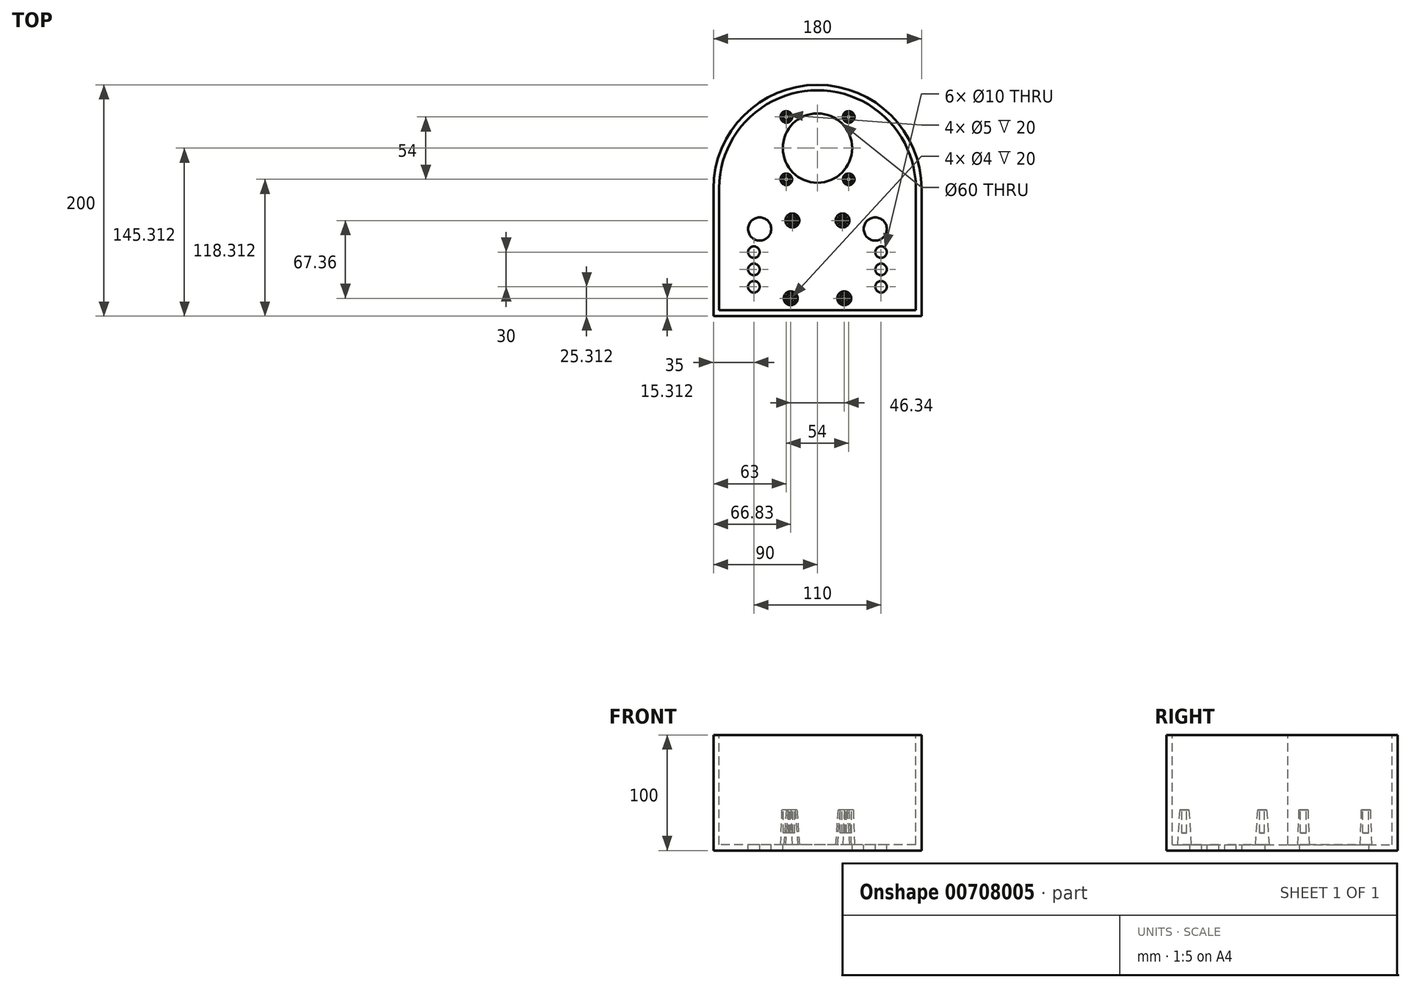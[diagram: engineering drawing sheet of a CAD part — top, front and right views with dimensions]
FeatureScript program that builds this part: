
annotation { "Feature Type Name" : "Feature", "Feature Type Description" : "" }
export const myFeature = defineFeature(function(context is Context, id is Id, definition is map)
    precondition{}
    {
        {
            var Q0;
            Q0=qCreatedBy(makeId("Top.planeOp"),FACE);
            var sketch = newSketch(context, id + "F0", { "sketchPlane" : qUnion([Q0])});
            skLineSegment(sketch, "E0.bottom", {"start": v(90, -55) * mm, "end": v(-90, -55) * mm});
            skLineSegment(sketch, "E0.top", {"start": v(90, 55) * mm, "end": v(-90, 55) * mm});
            skLineSegment(sketch, "E0.left", {"start": v(90, -55) * mm, "end": v(90, 55) * mm});
            skLineSegment(sketch, "E0.right", {"start": v(-90, -55) * mm, "end": v(-90, 55) * mm});
            skPoint(sketch, "E0.middle", {"position": v(0, 0) * mm});
            skArc(sketch, "E1", {"start": v(90, 55) * mm, "mid": v(0, 145) * mm, "end": v(-90, 55) * mm});
            skSolve(sketch);
        }
        {
            var Q0;
            Q0 = qSketchRegion(id + "F0", true);
            extrude(context, id + "F1", {"entities" : qUnion([Q0]), "depth" : 100 * mm, "offsetDistance" : 25 * mm});
        }
        {
            var Q0;
            Q0=makeQuery(id+"F1.opExtrude","CAP_FACE",FACE,{"disambiguationData":[OSD([sQuery(id+"F0.wireOp",EDGE,"E0.bottom"),sQuery(id+"F0.wireOp",EDGE,"E0.left"),sQuery(id+"F0.wireOp",EDGE,"E0.right"),sQuery(id+"F0.wireOp",EDGE,"E1")])],"isStart":false});
            var sketch = newSketch(context, id + "F2", { "sketchPlane" : qUnion([Q0])});
            skLineSegment(sketch, "E2.bottom", {"start": v(85, -50) * mm, "end": v(-85, -50) * mm});
            skLineSegment(sketch, "E2.top", {"start": v(85, 50) * mm, "end": v(-85, 50) * mm});
            skLineSegment(sketch, "E2.left", {"start": v(85, -50) * mm, "end": v(85, 50) * mm});
            skLineSegment(sketch, "E2.right", {"start": v(-85, -50) * mm, "end": v(-85, 50) * mm});
            skPoint(sketch, "E2.middle", {"position": v(0, 0) * mm});
            skArc(sketch, "E3", {"start": v(85, 50) * mm, "mid": v(0, 140.31) * mm, "end": v(-85, 50) * mm});
            skSolve(sketch);
        }
        {
            var Q0;
            Q0 = qSketchRegion(id + "F2", true);
            extrude(context, id + "F3", {"entities" : qUnion([Q0]), "operationType" : NewBodyOperationType.REMOVE, "oppositeDirection" : true, "depth" : 95 * mm, "offsetDistance" : 25 * mm});
        }
        {
            var Q0;
            Q0=makeQuery(id+"F3.boolean.opBoolean","COPY",FACE,{"derivedFrom":makeQuery(id+"F3.opExtrude","CAP_FACE",FACE,{"disambiguationData":[OSD([sQuery(id+"F2.wireOp",EDGE,"E2.bottom"),sQuery(id+"F2.wireOp",EDGE,"E2.left"),sQuery(id+"F2.wireOp",EDGE,"E2.right"),sQuery(id+"F2.wireOp",EDGE,"E3")])],"isStart":false})});
            var sketch = newSketch(context, id + "F4", { "sketchPlane" : qUnion([Q0])});
            skCircle(sketch, "E4", {"center": v(0, 90.31) * mm, "radius": 30 * mm});
            skCircle(sketch, "E5", {"center": v(-55, 0.31) * mm, "radius": 5 * mm});
            skCircle(sketch, "E6", {"center": v(-55, -14.69) * mm, "radius": 5 * mm});
            skCircle(sketch, "E7", {"center": v(55, 0.31) * mm, "radius": 5 * mm});
            skCircle(sketch, "E8", {"center": v(55, -14.69) * mm, "radius": 5 * mm});
            skCircle(sketch, "E9", {"center": v(-50, 20.31) * mm, "radius": 10 * mm});
            skCircle(sketch, "E10", {"center": v(50, 20.31) * mm, "radius": 10 * mm});
            skCircle(sketch, "E11", {"center": v(-55, -29.69) * mm, "radius": 5 * mm});
            skCircle(sketch, "E12", {"center": v(55, -29.69) * mm, "radius": 5 * mm});
            skSolve(sketch);
        }
        {
            var Q0;
            Q0 = qSketchRegion(id + "F4", true);
            extrude(context, id + "F5", {"entities" : qUnion([Q0]), "operationType" : NewBodyOperationType.REMOVE, "endBound" : BoundingType.THROUGH_ALL, "oppositeDirection" : true, "depth" : 25 * mm, "offsetDistance" : 25 * mm});
        }
        {
            var Q0;
            Q0=makeQuery(id+"F3.boolean.opBoolean","COPY",FACE,{"derivedFrom":makeQuery(id+"F3.opExtrude","CAP_FACE",FACE,{"disambiguationData":[OSD([sQuery(id+"F2.wireOp",EDGE,"E2.bottom"),sQuery(id+"F2.wireOp",EDGE,"E2.left"),sQuery(id+"F2.wireOp",EDGE,"E2.right"),sQuery(id+"F2.wireOp",EDGE,"E3")])],"isStart":false})});
            var sketch = newSketch(context, id + "F6", { "sketchPlane" : qUnion([Q0])});
            skCircle(sketch, "E13", {"center": v(-21.67, 27.67) * mm, "radius": 6 * mm});
            skPoint(sketch, "E14.middle", {"position": v(0, -16.82) * mm});
            skCircle(sketch, "E15", {"center": v(21.67, 27.67) * mm, "radius": 6 * mm});
            skCircle(sketch, "E16", {"center": v(-23.17, -39.69) * mm, "radius": 6 * mm});
            skCircle(sketch, "E17", {"center": v(23.17, -39.69) * mm, "radius": 6 * mm});
            skCircle(sketch, "E18", {"center": v(27, 63.31) * mm, "radius": 5 * mm});
            skCircle(sketch, "E19", {"center": v(27, 117.31) * mm, "radius": 5 * mm});
            skCircle(sketch, "E20", {"center": v(-27, 117.31) * mm, "radius": 5 * mm});
            skCircle(sketch, "E21", {"center": v(-27, 63.31) * mm, "radius": 5 * mm});
            skSolve(sketch);
        }
        {
            var Q0;
            Q0=makeQuery(id+"F6.imprint","IMPRINT",FACE,{"disambiguationData":[TD([[makeQuery(id+"F6.imprint","IMPRINT",EDGE,{"derivedFrom":sQuery(id+"F6.wireOp",EDGE,"E13")}),-1.0]])]});
            cPlane(context, id + "F7", {"entities" : qUnion([Q0]), "cplaneType" : CPlaneType.OFFSET, "offset" : 30 * mm, "width" : 150 * mm, "height" : 150 * mm});
        }
        {
            var Q0;
            Q0=qCreatedBy(id+"F7.planeOp",FACE);
            var sketch = newSketch(context, id + "F8", { "sketchPlane" : qUnion([Q0])});
            skCircle(sketch, "E22", {"center": v(-21.67, 27.67) * mm, "radius": 4 * mm});
            skCircle(sketch, "E23", {"center": v(21.67, 27.67) * mm, "radius": 4 * mm});
            skCircle(sketch, "E24", {"center": v(23.17, -39.69) * mm, "radius": 4 * mm});
            skCircle(sketch, "E25", {"center": v(-23.17, -39.69) * mm, "radius": 4 * mm});
            skCircle(sketch, "E26", {"center": v(27, 63.31) * mm, "radius": 4 * mm});
            skCircle(sketch, "E27", {"center": v(27, 117.31) * mm, "radius": 4 * mm});
            skCircle(sketch, "E28", {"center": v(-27, 63.31) * mm, "radius": 4 * mm});
            skCircle(sketch, "E29", {"center": v(-27, 117.31) * mm, "radius": 4 * mm});
            skSolve(sketch);
        }
        {
            var Q1;
            Q1=makeQuery(id+"F6.imprint","IMPRINT",FACE,{"disambiguationData":[TD([[makeQuery(id+"F6.imprint","IMPRINT",EDGE,{"derivedFrom":sQuery(id+"F6.wireOp",EDGE,"E13")}),1.0]])]});
            var Q2;
            Q2=makeQuery(id+"F8.imprint","IMPRINT",FACE,{"disambiguationData":[TD([[makeQuery(id+"F8.imprint","IMPRINT",EDGE,{"derivedFrom":sQuery(id+"F8.wireOp",EDGE,"E22")}),1.0]])]});
            loft(context, id + "F9", {"operationType" : NewBodyOperationType.ADD, "sheetProfilesArray" : [{ "sheetProfileEntities" : qUnion([Q1]) }, { "sheetProfileEntities" : qUnion([Q2]) }]});
        }
        {
            var Q1;
            Q1=makeQuery(id+"F6.imprint","IMPRINT",FACE,{"disambiguationData":[TD([[makeQuery(id+"F6.imprint","IMPRINT",EDGE,{"derivedFrom":sQuery(id+"F6.wireOp",EDGE,"E15")}),1.0]])]});
            var Q2;
            Q2=makeQuery(id+"F8.imprint","IMPRINT",FACE,{"disambiguationData":[TD([[makeQuery(id+"F8.imprint","IMPRINT",EDGE,{"derivedFrom":sQuery(id+"F8.wireOp",EDGE,"E23")}),1.0]])]});
            loft(context, id + "F10", {"operationType" : NewBodyOperationType.ADD, "sheetProfilesArray" : [{ "sheetProfileEntities" : qUnion([Q1]) }, { "sheetProfileEntities" : qUnion([Q2]) }]});
        }
        {
            var Q1;
            Q1=makeQuery(id+"F6.imprint","IMPRINT",FACE,{"disambiguationData":[TD([[makeQuery(id+"F6.imprint","IMPRINT",EDGE,{"derivedFrom":sQuery(id+"F6.wireOp",EDGE,"E16")}),1.0]])]});
            var Q2;
            Q2=makeQuery(id+"F8.imprint","IMPRINT",FACE,{"disambiguationData":[TD([[makeQuery(id+"F8.imprint","IMPRINT",EDGE,{"derivedFrom":sQuery(id+"F8.wireOp",EDGE,"E25")}),1.0]])]});
            loft(context, id + "F11", {"operationType" : NewBodyOperationType.ADD, "sheetProfilesArray" : [{ "sheetProfileEntities" : qUnion([Q1]) }, { "sheetProfileEntities" : qUnion([Q2]) }]});
        }
        {
            var Q1;
            Q1=makeQuery(id+"F6.imprint","IMPRINT",FACE,{"disambiguationData":[TD([[makeQuery(id+"F6.imprint","IMPRINT",EDGE,{"derivedFrom":sQuery(id+"F6.wireOp",EDGE,"E17")}),1.0]])]});
            var Q2;
            Q2=makeQuery(id+"F8.imprint","IMPRINT",FACE,{"disambiguationData":[TD([[makeQuery(id+"F8.imprint","IMPRINT",EDGE,{"derivedFrom":sQuery(id+"F8.wireOp",EDGE,"E24")}),1.0]])]});
            loft(context, id + "F12", {"operationType" : NewBodyOperationType.ADD, "sheetProfilesArray" : [{ "sheetProfileEntities" : qUnion([Q1]) }, { "sheetProfileEntities" : qUnion([Q2]) }]});
        }
        {
            var Q0;
            Q0=makeQuery(id+"F8.imprint","IMPRINT",FACE,{"disambiguationData":[TD([[makeQuery(id+"F8.imprint","IMPRINT",EDGE,{"derivedFrom":sQuery(id+"F8.wireOp",EDGE,"E22")}),1.0]])]});
            var sketch = newSketch(context, id + "F13", { "sketchPlane" : qUnion([Q0])});
            skCircle(sketch, "E30", {"center": v(-21.67, 27.67) * mm, "radius": 2 * mm});
            skCircle(sketch, "E31", {"center": v(21.67, 27.67) * mm, "radius": 2 * mm});
            skCircle(sketch, "E32", {"center": v(23.17, -39.69) * mm, "radius": 2 * mm});
            skCircle(sketch, "E33", {"center": v(-23.17, -39.69) * mm, "radius": 2 * mm});
            skPoint(sketch, "E34.middle", {"position": v(0, 90.31) * mm});
            skCircle(sketch, "E35", {"center": v(27, 63.31) * mm, "radius": 2.5 * mm});
            skCircle(sketch, "E36", {"center": v(27, 117.31) * mm, "radius": 2.5 * mm});
            skCircle(sketch, "E37", {"center": v(-27, 63.31) * mm, "radius": 2.5 * mm});
            skCircle(sketch, "E38", {"center": v(-27, 117.31) * mm, "radius": 2.5 * mm});
            skSolve(sketch);
        }
        {
            var Q1;
            Q1=makeQuery(id+"F6.imprint","IMPRINT",FACE,{"disambiguationData":[TD([[makeQuery(id+"F6.imprint","IMPRINT",EDGE,{"derivedFrom":sQuery(id+"F6.wireOp",EDGE,"E19")}),1.0]])]});
            var Q2;
            Q2=makeQuery(id+"F8.imprint","IMPRINT",FACE,{"disambiguationData":[TD([[makeQuery(id+"F8.imprint","IMPRINT",EDGE,{"derivedFrom":sQuery(id+"F8.wireOp",EDGE,"E27")}),1.0]])]});
            loft(context, id + "F14", {"operationType" : NewBodyOperationType.ADD, "sheetProfilesArray" : [{ "sheetProfileEntities" : qUnion([Q1]) }, { "sheetProfileEntities" : qUnion([Q2]) }]});
        }
        {
            var Q1;
            Q1=makeQuery(id+"F6.imprint","IMPRINT",FACE,{"disambiguationData":[TD([[makeQuery(id+"F6.imprint","IMPRINT",EDGE,{"derivedFrom":sQuery(id+"F6.wireOp",EDGE,"E18")}),1.0]])]});
            var Q2;
            Q2=makeQuery(id+"F8.imprint","IMPRINT",FACE,{"disambiguationData":[TD([[makeQuery(id+"F8.imprint","IMPRINT",EDGE,{"derivedFrom":sQuery(id+"F8.wireOp",EDGE,"E26")}),1.0]])]});
            loft(context, id + "F15", {"operationType" : NewBodyOperationType.ADD, "sheetProfilesArray" : [{ "sheetProfileEntities" : qUnion([Q1]) }, { "sheetProfileEntities" : qUnion([Q2]) }]});
        }
        {
            var Q1;
            Q1=makeQuery(id+"F6.imprint","IMPRINT",FACE,{"disambiguationData":[TD([[makeQuery(id+"F6.imprint","IMPRINT",EDGE,{"derivedFrom":sQuery(id+"F6.wireOp",EDGE,"E21")}),1.0]])]});
            var Q2;
            Q2=makeQuery(id+"F8.imprint","IMPRINT",FACE,{"disambiguationData":[TD([[makeQuery(id+"F8.imprint","IMPRINT",EDGE,{"derivedFrom":sQuery(id+"F8.wireOp",EDGE,"E28")}),1.0]])]});
            loft(context, id + "F16", {"operationType" : NewBodyOperationType.ADD, "sheetProfilesArray" : [{ "sheetProfileEntities" : qUnion([Q1]) }, { "sheetProfileEntities" : qUnion([Q2]) }]});
        }
        {
            var Q1;
            Q1=makeQuery(id+"F6.imprint","IMPRINT",FACE,{"disambiguationData":[TD([[makeQuery(id+"F6.imprint","IMPRINT",EDGE,{"derivedFrom":sQuery(id+"F6.wireOp",EDGE,"E20")}),1.0]])]});
            var Q2;
            Q2=makeQuery(id+"F8.imprint","IMPRINT",FACE,{"disambiguationData":[TD([[makeQuery(id+"F8.imprint","IMPRINT",EDGE,{"derivedFrom":sQuery(id+"F8.wireOp",EDGE,"E29")}),1.0]])]});
            loft(context, id + "F17", {"operationType" : NewBodyOperationType.ADD, "sheetProfilesArray" : [{ "sheetProfileEntities" : qUnion([Q1]) }, { "sheetProfileEntities" : qUnion([Q2]) }]});
        }
        {
            var Q0;
            Q0 = qSketchRegion(id + "F13", true);
            extrude(context, id + "F18", {"entities" : qUnion([Q0]), "operationType" : NewBodyOperationType.REMOVE, "oppositeDirection" : true, "depth" : 20 * mm, "offsetDistance" : 25 * mm});
        }
    });
